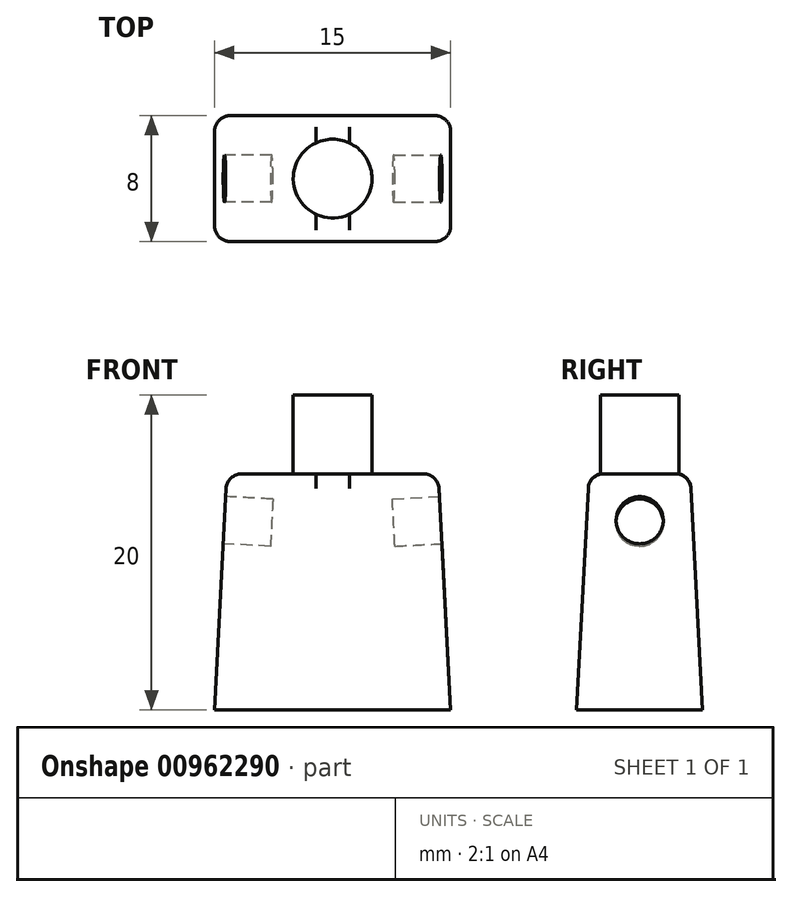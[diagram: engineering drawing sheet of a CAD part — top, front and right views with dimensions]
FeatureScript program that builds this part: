
annotation { "Feature Type Name" : "Feature", "Feature Type Description" : "" }
export const myFeature = defineFeature(function(context is Context, id is Id, definition is map)
    precondition{}
    {
        {
            var Q0;
            Q0=qCreatedBy(makeId("Top.planeOp"),FACE);
            var sketch = newSketch(context, id + "F0", { "sketchPlane" : qUnion([Q0])});
            skLineSegment(sketch, "E0.bottom", {"start": v(7.5, -4) * mm, "end": v(-7.5, -4) * mm});
            skLineSegment(sketch, "E0.top", {"start": v(7.5, 4) * mm, "end": v(-7.5, 4) * mm});
            skLineSegment(sketch, "E0.left", {"start": v(7.5, -4) * mm, "end": v(7.5, 4) * mm});
            skLineSegment(sketch, "E0.right", {"start": v(-7.5, -4) * mm, "end": v(-7.5, 4) * mm});
            skPoint(sketch, "E0.middle", {"position": v(0, 0) * mm});
            skSolve(sketch);
        }
        {
            var Q0;
            Q0 = qSketchRegion(id + "F0", true);
            extrude(context, id + "F1", {"entities" : qUnion([Q0]), "depth" : 15 * mm, "offsetDistance" : 25 * mm, "hasDraft" : true, "draftAngle" : 3 * degree, "draftPullDirection" : true});
        }
        {
            var Q0;
            Q0=makeQuery(id+"F1.opExtrude","CAP_FACE",FACE,{"disambiguationData":[OSD([sQuery(id+"F0.wireOp",EDGE,"E0.bottom"),sQuery(id+"F0.wireOp",EDGE,"E0.top"),sQuery(id+"F0.wireOp",EDGE,"E0.left"),sQuery(id+"F0.wireOp",EDGE,"E0.right")])],"isStart":false});
            var sketch = newSketch(context, id + "F2", { "sketchPlane" : qUnion([Q0])});
            skCircle(sketch, "E1", {"center": v(0, 0) * mm, "radius": 2.5 * mm});
            skSolve(sketch);
        }
        {
            var Q0;
            Q0 = qSketchRegion(id + "F2", true);
            extrude(context, id + "F3", {"entities" : qUnion([Q0]), "operationType" : NewBodyOperationType.ADD, "depth" : 5 * mm, "offsetDistance" : 25 * mm});
        }
        {
            var Q0;
            Q0=makeQuery(id+"F1.opExtrude","SWEPT_EDGE",EDGE,{"disambiguationData":[OSD([sQuery(id+"F0.wireOp",EDGE,"E0.bottom"),sQuery(id+"F0.wireOp",EDGE,"E0.right")])]});
            var Q1;
            Q1=makeQuery(id+"F1.opExtrude","SWEPT_EDGE",EDGE,{"disambiguationData":[OSD([sQuery(id+"F0.wireOp",EDGE,"E0.bottom"),sQuery(id+"F0.wireOp",EDGE,"E0.left")])]});
            var Q2;
            Q2=makeQuery(id+"F1.opExtrude","SWEPT_EDGE",EDGE,{"disambiguationData":[OSD([sQuery(id+"F0.wireOp",EDGE,"E0.top"),sQuery(id+"F0.wireOp",EDGE,"E0.left")])]});
            var Q3;
            Q3=makeQuery(id+"F1.opExtrude","CAP_EDGE",EDGE,{"disambiguationData":[OSD([sQuery(id+"F0.wireOp",EDGE,"E0.left")])],"isStart":false});
            var Q4;
            Q4=makeQuery(id+"F1.opExtrude","CAP_EDGE",EDGE,{"disambiguationData":[OSD([sQuery(id+"F0.wireOp",EDGE,"E0.bottom")])],"isStart":false});
            var Q5;
            Q5=makeQuery(id+"F1.opExtrude","CAP_EDGE",EDGE,{"disambiguationData":[OSD([sQuery(id+"F0.wireOp",EDGE,"E0.right")])],"isStart":false});
            var Q6;
            Q6=makeQuery(id+"F1.opExtrude","CAP_EDGE",EDGE,{"disambiguationData":[OSD([sQuery(id+"F0.wireOp",EDGE,"E0.top")])],"isStart":false});
            var Q7;
            Q7=makeQuery(id+"F1.opExtrude","SWEPT_EDGE",EDGE,{"disambiguationData":[OSD([sQuery(id+"F0.wireOp",EDGE,"E0.top"),sQuery(id+"F0.wireOp",EDGE,"E0.right")])]});
            fillet(context, id + "F4", {"entities" : qUnion([Q0, Q1, Q2, Q3, Q4, Q5, Q6, Q7]), "radius" : 1 * mm, "tangentPropagation" : true, "allowEdgeOverflow" : false});
        }
        {
            var Q0;
            Q0=makeQuery(id+"F1.opExtrude","SWEPT_FACE",FACE,{"disambiguationData":[OSD([sQuery(id+"F0.wireOp",EDGE,"E0.right")])]});
            var sketch = newSketch(context, id + "F5", { "sketchPlane" : qUnion([Q0])});
            skCircle(sketch, "E2", {"center": v(0, 11.68) * mm, "radius": 1.5 * mm});
            skSolve(sketch);
        }
        {
            var Q0;
            Q0 = qSketchRegion(id + "F5", true);
            extrude(context, id + "F6", {"entities" : qUnion([Q0]), "operationType" : NewBodyOperationType.REMOVE, "oppositeDirection" : true, "depth" : 3 * mm, "offsetDistance" : 25 * mm});
        }
        {
            var Q0;
            Q0=makeQuery(id+"F1.opExtrude","SWEPT_FACE",FACE,{"disambiguationData":[OSD([sQuery(id+"F0.wireOp",EDGE,"E0.left")])]});
            var sketch = newSketch(context, id + "F7", { "sketchPlane" : qUnion([Q0])});
            skCircle(sketch, "E3", {"center": v(0, 11.68) * mm, "radius": 1.5 * mm});
            skSolve(sketch);
        }
        {
            var Q0;
            Q0 = qSketchRegion(id + "F7", true);
            extrude(context, id + "F8", {"entities" : qUnion([Q0]), "operationType" : NewBodyOperationType.REMOVE, "oppositeDirection" : true, "depth" : 3 * mm, "offsetDistance" : 25 * mm});
        }
    });
